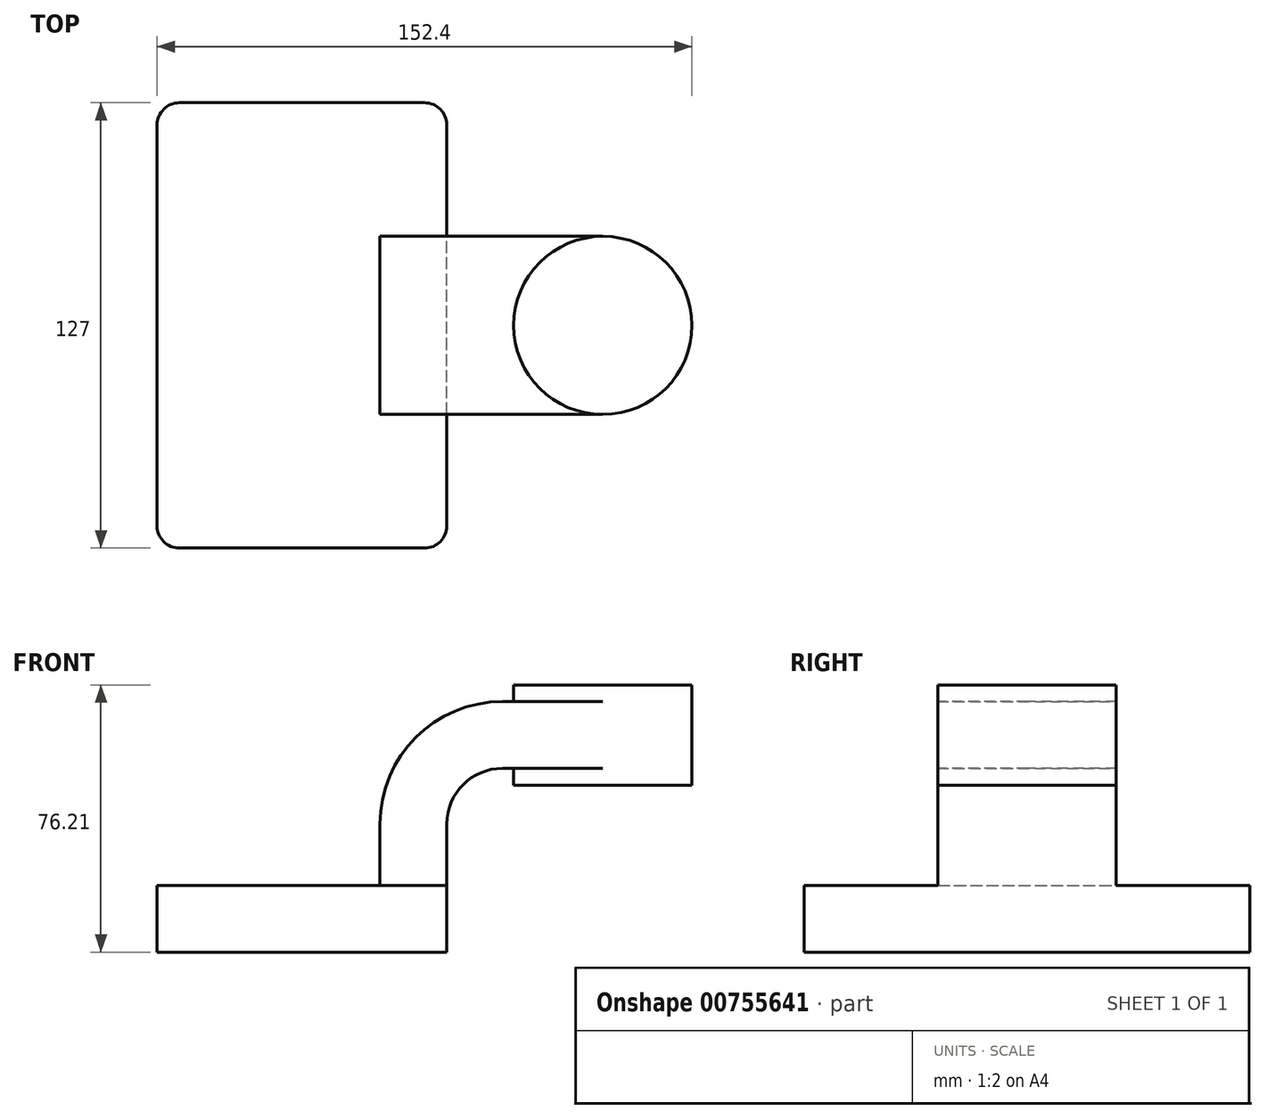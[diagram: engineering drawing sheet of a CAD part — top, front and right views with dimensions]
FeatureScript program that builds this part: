
annotation { "Feature Type Name" : "Feature", "Feature Type Description" : "" }
export const myFeature = defineFeature(function(context is Context, id is Id, definition is map)
    precondition{}
    {
        {
            var Q0;
            Q0=qCreatedBy(makeId("Front.planeOp"),FACE);
            var sketch = newSketch(context, id + "F0", { "sketchPlane" : qUnion([Q0])});
            skLineSegment(sketch, "E0.bottom", {"start": v(41.28, -9.52) * mm, "end": v(-41.28, -9.53) * mm});
            skLineSegment(sketch, "E0.top", {"start": v(41.28, 9.53) * mm, "end": v(-41.28, 9.53) * mm});
            skLineSegment(sketch, "E0.left", {"start": v(41.28, -9.52) * mm, "end": v(41.28, 9.53) * mm});
            skLineSegment(sketch, "E0.right", {"start": v(-41.28, -9.53) * mm, "end": v(-41.28, 9.53) * mm});
            skPoint(sketch, "E0.middle", {"position": v(0, 0) * mm});
            skLineSegment(sketch, "E1.bottom", {"start": v(111.12, 38.1) * mm, "end": v(60.32, 38.1) * mm});
            skLineSegment(sketch, "E1.top", {"start": v(111.12, 66.68) * mm, "end": v(60.32, 66.68) * mm});
            skLineSegment(sketch, "E1.left", {"start": v(111.12, 38.1) * mm, "end": v(111.12, 66.68) * mm});
            skLineSegment(sketch, "E1.right", {"start": v(60.32, 38.1) * mm, "end": v(60.32, 66.68) * mm});
            skPoint(sketch, "E1.middle", {"position": v(85.72, 52.39) * mm});
            skLineSegment(sketch, "E2", {"start": v(41.28, 9.53) * mm, "end": v(41.28, 27) * mm});
            skArc(sketch, "E3", {"start": v(41.27, 27) * mm, "mid": v(45.92, 38.23) * mm, "end": v(57.15, 42.88) * mm});
            skLineSegment(sketch, "E4", {"start": v(57.15, 42.88) * mm, "end": v(85.72, 42.88) * mm});
            skLineSegment(sketch, "E5.0", {"start": v(57.15, 61.93) * mm, "end": v(85.72, 61.93) * mm});
            skArc(sketch, "E5.1", {"start": v(22.23, 27) * mm, "mid": v(32.45, 51.7) * mm, "end": v(57.15, 61.93) * mm});
            skLineSegment(sketch, "E5.2", {"start": v(22.23, 9.53) * mm, "end": v(22.23, 27) * mm});
            skLineSegment(sketch, "E6", {"start": v(85.72, 38.1) * mm, "end": v(85.72, 66.68) * mm});
            skFitSpline(sketch, "E7", {"points": [v(-41.28, 9.53) * mm, v(57.15, 61.93) * mm], "startDerivative": vector(15.48, 82.3) * mm, "endDerivative": vector(147.42, -9.4) * mm});
            skSolve(sketch);
        }
        {
            var Q0;
            Q0=makeQuery(id+"F0.imprint","IMPRINT",FACE,{"disambiguationData":[TD([[makeQuery(id+"F0.imprint","IMPRINT",EDGE,{"derivedFrom":sQuery(id+"F0.wireOp",EDGE,"E0.bottom")}),-1.0]])]});
            extrude(context, id + "F1", {"entities" : qUnion([Q0]), "endBound" : BoundingType.SYMMETRIC, "depth" : 127 * mm, "offsetDistance" : 25.4 * mm});
        }
        {
            var Q0;
            {var subQ1=sQuery(id+"F0.wireOp",EDGE,"E2");Q0=makeQuery(id+"F0.imprint","IMPRINT",FACE,{"disambiguationData":[TD([[makeQuery(id+"F0.imprint","IMPRINT",EDGE,{"derivedFrom":subQ1}),1.0]])]});}
            extrude(context, id + "F2", {"entities" : qUnion([Q0]), "operationType" : NewBodyOperationType.ADD, "endBound" : BoundingType.SYMMETRIC, "depth" : 50.8 * mm, "offsetDistance" : 25.4 * mm});
        }
        {
            var Q0;
            Q0=makeQuery(id+"F0.imprint","IMPRINT",FACE,{"disambiguationData":[TD([[makeQuery(id+"F0.imprint","IMPRINT",EDGE,{"derivedFrom":sQuery(id+"F0.wireOp",EDGE,"E5.1")}),1.0]])]});
            extrude(context, id + "F3", {"entities" : qUnion([Q0]), "operationType" : NewBodyOperationType.ADD, "endBound" : BoundingType.SYMMETRIC, "depth" : 15.88 * mm, "offsetDistance" : 25.4 * mm});
        }
        {
            var Q0;
            {var subQ0=sQuery(id+"F0.wireOp",EDGE,"E4");var subQ1=sQuery(id+"F0.wireOp",EDGE,"E1.right");var subQ2=makeQuery(id+"F0.imprint","INTERSECT",VERTEX,{"derivedFrom":[subQ1,subQ0]});Q0=makeQuery(id+"F0.imprint","IMPRINT",FACE,{"disambiguationData":[TD([[makeQuery(id+"F0.imprint","IMPRINT",EDGE,{"disambiguationData":[TD([[subQ2,-1.0]])],"derivedFrom":subQ1}),-1.0]])]});}
            extrude(context, id + "F4", {"entities" : qUnion([Q0]), "operationType" : NewBodyOperationType.ADD, "endBound" : BoundingType.SYMMETRIC, "depth" : 50.8 * mm, "offsetDistance" : 25.4 * mm});
        }
        {
            var Q0;
            {var subQ4=sQuery(id+"F0.wireOp",EDGE,"E1.left");Q0=makeQuery(id+"F0.imprint","IMPRINT",FACE,{"disambiguationData":[TD([[makeQuery(id+"F0.imprint","IMPRINT",EDGE,{"derivedFrom":subQ4}),1.0]])]});}
            var Q1;
            Q1=sQuery(id+"F0.wireOp",EDGE,"E6");
            revolve(context, id + "F5", {"operationType" : NewBodyOperationType.ADD, "surfaceOperationType" : NewSurfaceOperationType.NEW, "entities" : qUnion([Q0]), "axis" : qUnion([Q1]), "revolveType" : RevolveType.FULL});
        }
        {
            var Q0;
            Q0=makeQuery(id+"F1.opExtrude","CAP_EDGE",EDGE,{"disambiguationData":[OSD([sQuery(id+"F0.wireOp",EDGE,"E0.left")])],"isStart":false});
            var Q1;
            Q1=makeQuery(id+"F1.opExtrude","CAP_EDGE",EDGE,{"disambiguationData":[OSD([sQuery(id+"F0.wireOp",EDGE,"E0.right")])],"isStart":false});
            var Q2;
            Q2=makeQuery(id+"F1.opExtrude","CAP_EDGE",EDGE,{"disambiguationData":[OSD([sQuery(id+"F0.wireOp",EDGE,"E0.left")])],"isStart":true});
            var Q3;
            Q3=makeQuery(id+"F1.opExtrude","CAP_EDGE",EDGE,{"disambiguationData":[OSD([sQuery(id+"F0.wireOp",EDGE,"E0.right")])],"isStart":true});
            fillet(context, id + "F6", {"entities" : qUnion([Q0, Q1, Q2, Q3]), "radius" : 6.35 * mm, "tangentPropagation" : true, "allowEdgeOverflow" : false});
        }
    });
